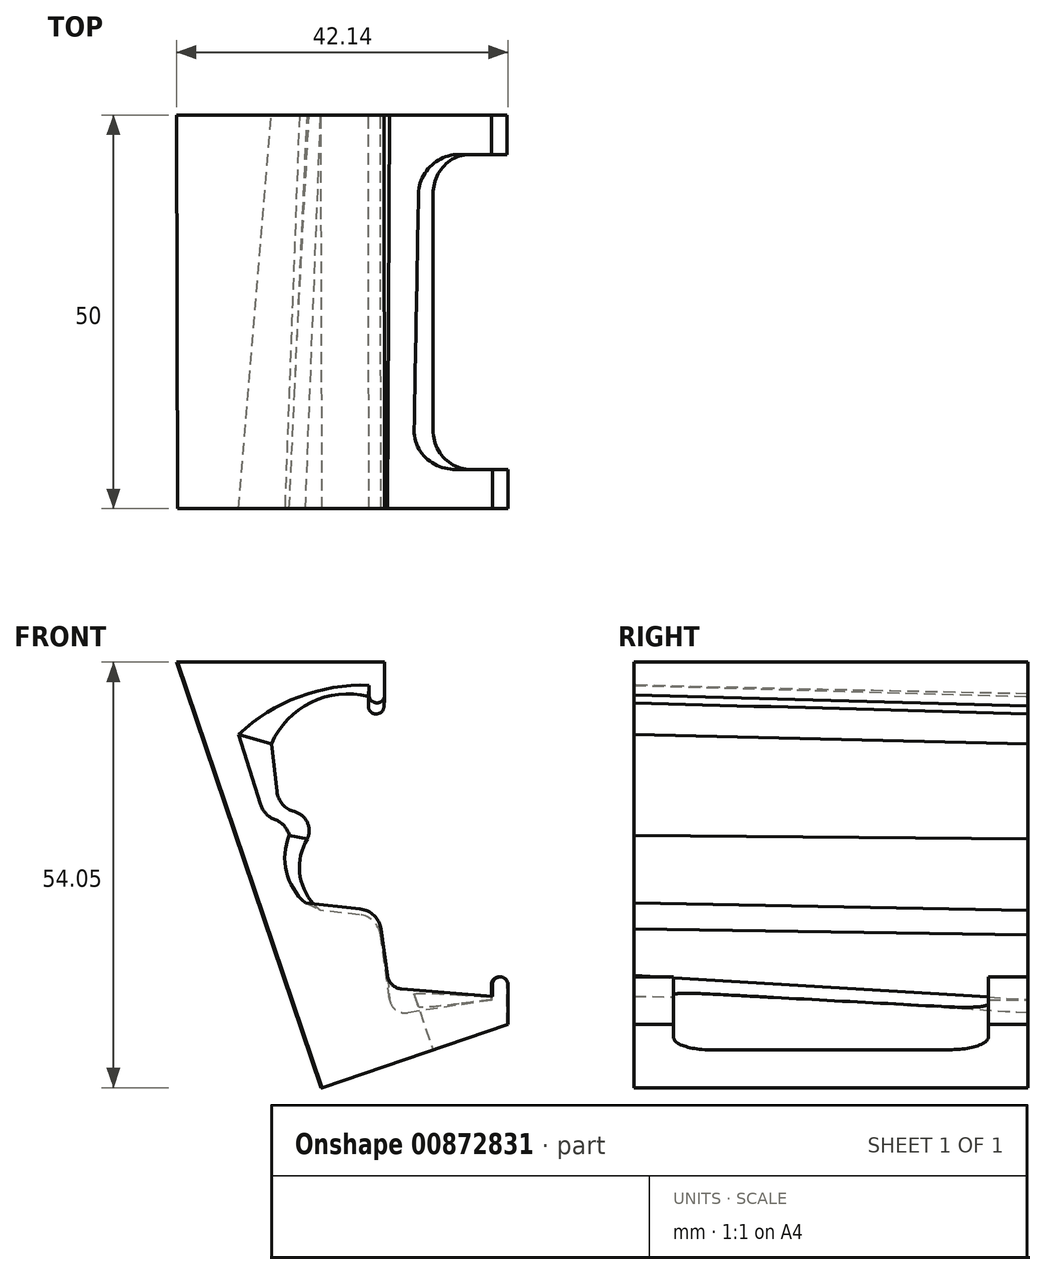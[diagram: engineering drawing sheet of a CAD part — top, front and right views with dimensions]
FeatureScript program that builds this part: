
annotation { "Feature Type Name" : "Feature", "Feature Type Description" : "" }
export const myFeature = defineFeature(function(context is Context, id is Id, definition is map)
    precondition{}
    {
        {
            var Q0;
            Q0=qCreatedBy(makeId("Front.planeOp"),FACE);
            var sketch = newSketch(context, id + "F0", { "sketchPlane" : qUnion([Q0])});
            skLineSegment(sketch, "E0", {"start": v(26.78, 18.86) * mm, "end": v(26.78, -18.67) * mm, "construction": true});
            skFitSpline(sketch, "E1", {"points": [v(2.02, 19.06) * mm, v(0.43, 19.96) * mm, v(-2.84, 19.7) * mm, v(-7.3, 17.92) * mm, v(-11.02, 14.63) * mm, v(-11.52, 11.68) * mm, v(-11.12, 8.55) * mm, v(-10.27, 5.2) * mm, v(-9.23, 3.76) * mm, v(-8.1, 2.95) * mm, v(-7.5, 1.72) * mm, v(-7.46, -0.5) * mm, v(-7.8, -1.76) * mm, v(-7.9, -3.2) * mm, v(-7.44, -5.3) * mm, v(-5.37, -8.08) * mm, v(-3.03, -8.65) * mm, v(-1.6, -8.65) * mm, v(0, -8.76) * mm, v(1.6, -9.26) * mm, v(2.84, -10.63) * mm, v(3.46, -12.42) * mm, v(3.56, -13.7) * mm, v(3.7, -15.6) * mm, v(4.15, -17.72) * mm, v(4.7, -18.85) * mm, v(8.8, -19.5) * mm, v(14.65, -19.88) * mm], "startDerivative": vector(-47.97, 57.65) * mm, "endDerivative": vector(98.98, -5.54) * mm});
            skSolve(sketch);
        }
        {
            var Q0;
            Q0=qCreatedBy(makeId("Front.planeOp"),FACE);
            var sketch = newSketch(context, id + "F1", { "sketchPlane" : qUnion([Q0])});
            skFitSpline(sketch, "E2.0", {"points": [v(2.02, 19.06) * mm, v(1.5, 19.69) * mm, v(0.48, 20.13) * mm, v(-3.08, 19.87) * mm, v(-7.33, 18.2) * mm, v(-11.52, 14.95) * mm, v(-11.6, 11.64) * mm, v(-11.16, 8.62) * mm, v(-10.48, 5.18) * mm, v(-9.35, 3.7) * mm, v(-7.98, 3.04) * mm, v(-7.37, 1.75) * mm, v(-7.34, -0.53) * mm, v(-7.87, -1.72) * mm, v(-7.95, -3.28) * mm, v(-7.62, -5.37) * mm, v(-5.66, -8.49) * mm, v(-3.04, -8.68) * mm, v(-1.62, -8.63) * mm, v(0.02, -8.7) * mm, v(1.7, -9.1) * mm, v(2.96, -10.55) * mm, v(3.53, -12.41) * mm, v(3.55, -13.71) * mm, v(3.63, -15.62) * mm, v(4.17, -17.68) * mm, v(4.43, -19.3) * mm, v(9.19, -19.5) * mm, v(12.72, -19.77) * mm, v(14.65, -19.88) * mm]});
            skLineSegment(sketch, "E3", {"start": v(2.02, 19.06) * mm, "end": v(2.02, 19.06) * mm});
            skLineSegment(sketch, "E4", {"start": v(3.02, 18.06) * mm, "end": v(3.02, 18.06) * mm});
            skLineSegment(sketch, "E5", {"start": v(4.02, 19.06) * mm, "end": v(4.02, 19.46) * mm});
            skLineSegment(sketch, "E6", {"start": v(1.02, 22.46) * mm, "end": v(-22.37, 22.46) * mm});
            skLineSegment(sketch, "E7", {"start": v(-22.37, 22.46) * mm, "end": v(-4.04, -31.53) * mm});
            skPoint(sketch, "E8.visualSharp", {"position": v(2.02, 18.06) * mm});
            skArc(sketch, "E8.filletArc", {"start": v(2.02, 19.06) * mm, "mid": v(2.31, 18.36) * mm, "end": v(3.02, 18.06) * mm});
            skPoint(sketch, "E9.visualSharp", {"position": v(4.02, 18.06) * mm});
            skArc(sketch, "E9.filletArc", {"start": v(3.02, 18.06) * mm, "mid": v(3.73, 18.36) * mm, "end": v(4.02, 19.06) * mm});
            skPoint(sketch, "E10.visualSharp", {"position": v(4.02, 22.46) * mm});
            skArc(sketch, "E10.filletArc", {"start": v(4.02, 19.46) * mm, "mid": v(3.14, 21.58) * mm, "end": v(1.02, 22.46) * mm});
            skPoint(sketch, "E11.visualSharp", {"position": v(-22.37, 22.46) * mm});
            skLineSegment(sketch, "E12", {"start": v(-11.35, 21.09) * mm, "end": v(-11.35, 13.85) * mm, "construction": true});
            skLineSegment(sketch, "E13", {"start": v(14.65, -19.88) * mm, "end": v(17.63, -20.05) * mm});
            skLineSegment(sketch, "E14", {"start": v(19.63, -18.5) * mm, "end": v(19.63, -23.5) * mm});
            skLineSegment(sketch, "E15", {"start": v(19.63, -23.5) * mm, "end": v(-4.04, -31.53) * mm});
            skLineSegment(sketch, "E16", {"start": v(17.63, -20.05) * mm, "end": v(17.63, -18.5) * mm});
            skArc(sketch, "E17", {"start": v(19.63, -18.5) * mm, "mid": v(18.63, -17.5) * mm, "end": v(17.63, -18.5) * mm});
            skSolve(sketch);
        }
        {
            var Q0;
            Q0=qCreatedBy(makeId("Front.planeOp"),FACE);
            cPlane(context, id + "F2", {"entities" : qUnion([Q0]), "cplaneType" : CPlaneType.OFFSET, "offset" : 50 * mm, "width" : 150 * mm, "height" : 150 * mm});
        }
        {
            var Q0;
            Q0=qCreatedBy(makeId("Front.planeOp"),FACE);
            var sketch = newSketch(context, id + "F3", { "sketchPlane" : qUnion([Q0])});
            skLineSegment(sketch, "E18", {"start": v(17.62, -20.46) * mm, "end": v(7, -22.08) * mm});
            skLineSegment(sketch, "E19", {"start": v(4.71, -20.38) * mm, "end": v(3.56, -12.18) * mm});
            skLineSegment(sketch, "E20", {"start": v(0.92, -9.61) * mm, "end": v(-4.05, -9.06) * mm});
            skPoint(sketch, "E21.visualSharp", {"position": v(5, -22.39) * mm});
            skArc(sketch, "E21.filletArc", {"start": v(4.71, -20.38) * mm, "mid": v(5.5, -21.7) * mm, "end": v(7, -22.08) * mm});
            skPoint(sketch, "E22.visualSharp", {"position": v(3.23, -9.87) * mm});
            skArc(sketch, "E22.filletArc", {"start": v(3.56, -12.18) * mm, "mid": v(2.68, -10.44) * mm, "end": v(0.92, -9.61) * mm});
            skArc(sketch, "E23", {"start": v(-5.75, 0) * mm, "mid": v(-6.64, -4.86) * mm, "end": v(-4.05, -9.06) * mm});
            skLineSegment(sketch, "E24", {"start": v(-9.6, 6.03) * mm, "end": v(-10.31, 12.08) * mm});
            skArc(sketch, "E25", {"start": v(2, 18.13) * mm, "mid": v(-5.27, 17.37) * mm, "end": v(-10.31, 12.08) * mm});
            skArc(sketch, "E26", {"start": v(-5.75, 0) * mm, "mid": v(-5.75, 2.12) * mm, "end": v(-7.38, 3.48) * mm});
            skPoint(sketch, "E27.visualSharp", {"position": v(-9.27, 3.22) * mm});
            skArc(sketch, "E27.filletArc", {"start": v(-9.6, 6.03) * mm, "mid": v(-8.88, 4.42) * mm, "end": v(-7.38, 3.48) * mm});
            skLineSegment(sketch, "E28", {"start": v(17.62, -20.46) * mm, "end": v(17.62, -18.52) * mm});
            skLineSegment(sketch, "E29", {"start": v(19.62, -18.52) * mm, "end": v(19.62, -23.56) * mm});
            skLineSegment(sketch, "E30", {"start": v(19.62, -23.56) * mm, "end": v(-4.01, -31.58) * mm});
            skLineSegment(sketch, "E31", {"start": v(-4.01, -31.58) * mm, "end": v(-22.37, 22.47) * mm});
            skLineSegment(sketch, "E32", {"start": v(-22.37, 22.47) * mm, "end": v(4, 22.47) * mm});
            skArc(sketch, "E33", {"start": v(19.62, -18.52) * mm, "mid": v(18.62, -17.52) * mm, "end": v(17.62, -18.52) * mm});
            skLineSegment(sketch, "E34", {"start": v(4, 22.47) * mm, "end": v(4, 16.9) * mm});
            skLineSegment(sketch, "E35", {"start": v(2, 18.13) * mm, "end": v(2, 16.9) * mm});
            skArc(sketch, "E36", {"start": v(2, 16.9) * mm, "mid": v(3, 15.9) * mm, "end": v(4, 16.9) * mm});
            skSolve(sketch);
        }
        {
            var Q0;
            Q0=qCreatedBy(makeId("Front.planeOp"),FACE);
            cPlane(context, id + "F4", {"entities" : qUnion([Q0]), "cplaneType" : CPlaneType.OFFSET, "offset" : 50 * mm, "width" : 150 * mm, "height" : 150 * mm});
        }
        {
            var Q0;
            Q0=qCreatedBy(id+"F4.planeOp",FACE);
            var sketch = newSketch(context, id + "F5", { "sketchPlane" : qUnion([Q0])});
            skLineSegment(sketch, "E37", {"start": v(17.77, -20) * mm, "end": v(6.25, -19.05) * mm});
            skLineSegment(sketch, "E38", {"start": v(4.43, -17.34) * mm, "end": v(3.6, -11.44) * mm});
            skLineSegment(sketch, "E39", {"start": v(0.96, -8.88) * mm, "end": v(-5.98, -8.11) * mm});
            skPoint(sketch, "E40.visualSharp", {"position": v(4.66, -18.92) * mm});
            skArc(sketch, "E40.filletArc", {"start": v(4.43, -17.34) * mm, "mid": v(5.04, -18.51) * mm, "end": v(6.25, -19.05) * mm});
            skPoint(sketch, "E41.visualSharp", {"position": v(3.28, -9.14) * mm});
            skArc(sketch, "E41.filletArc", {"start": v(3.6, -11.44) * mm, "mid": v(2.72, -9.7) * mm, "end": v(0.96, -8.88) * mm});
            skArc(sketch, "E42", {"start": v(-8.04, 0.48) * mm, "mid": v(-8.4, -4.15) * mm, "end": v(-5.98, -8.11) * mm});
            skLineSegment(sketch, "E43", {"start": v(-11.7, 4.4) * mm, "end": v(-14.46, 13.3) * mm});
            skArc(sketch, "E44", {"start": v(-8.04, 0.48) * mm, "mid": v(-8.72, 1.7) * mm, "end": v(-9.88, 2.49) * mm});
            skPoint(sketch, "E45.visualSharp", {"position": v(-11.16, 2.67) * mm});
            skArc(sketch, "E45.filletArc", {"start": v(-11.7, 4.4) * mm, "mid": v(-11.01, 3.24) * mm, "end": v(-9.88, 2.49) * mm});
            skLineSegment(sketch, "E46", {"start": v(17.77, -20) * mm, "end": v(17.77, -18.52) * mm});
            skLineSegment(sketch, "E47", {"start": v(19.77, -18.52) * mm, "end": v(19.77, -23.56) * mm});
            skLineSegment(sketch, "E48", {"start": v(19.77, -23.56) * mm, "end": v(-3.86, -31.58) * mm});
            skLineSegment(sketch, "E49", {"start": v(-3.86, -31.58) * mm, "end": v(-22.22, 22.47) * mm});
            skLineSegment(sketch, "E50", {"start": v(-22.22, 22.47) * mm, "end": v(4.09, 22.47) * mm});
            skArc(sketch, "E51", {"start": v(19.77, -18.52) * mm, "mid": v(18.77, -17.52) * mm, "end": v(17.77, -18.52) * mm});
            skLineSegment(sketch, "E52", {"start": v(4.09, 22.47) * mm, "end": v(4.09, 18.3) * mm});
            skLineSegment(sketch, "E53", {"start": v(2.09, 19.54) * mm, "end": v(2.09, 18.3) * mm});
            skArc(sketch, "E54", {"start": v(2.09, 18.3) * mm, "mid": v(3.09, 17.3) * mm, "end": v(4.09, 18.3) * mm});
            skArc(sketch, "E55", {"start": v(2.09, 19.54) * mm, "mid": v(-6.8, 18.07) * mm, "end": v(-14.46, 13.3) * mm});
            skSolve(sketch);
        }
        {
            var Q0;
            Q0 = qSketchRegion(id + "F5", true);
            var Q1;
            Q1 = qSketchRegion(id + "F3", true);
            loft(context, id + "F6", {"sheetProfilesArray" : [{ "sheetProfileEntities" : qUnion([Q0]) }, { "sheetProfileEntities" : qUnion([Q1]) }]});
        }
        {
            var Q0;
            Q0=makeQuery(id+"F6.opLoft","SWEPT_FACE",FACE,{"disambiguationData":[OSD([sQuery(id+"F3.wireOp",EDGE,"E29"),sQuery(id+"F3.wireOp",EDGE,"E30"),sQuery(id+"F3.wireOp",EDGE,"E31"),sQuery(id+"F5.wireOp",EDGE,"E47"),sQuery(id+"F5.wireOp",EDGE,"E48"),sQuery(id+"F5.wireOp",EDGE,"E49")])]});
            var sketch = newSketch(context, id + "F7", { "sketchPlane" : qUnion([Q0])});
            skLineSegment(sketch, "E56", {"start": v(11.08, 25.02) * mm, "end": v(16.76, 25) * mm, "construction": true});
            skFitSpline(sketch, "E57.0.2", {"points": [v(10.73, 0.02) * mm, v(10.78, 16.69) * mm, v(10.83, 33.35) * mm, v(10.89, 50.02) * mm]});
            skLineSegment(sketch, "E58", {"start": v(13.08, 45.02) * mm, "end": v(12.96, 5.02) * mm});
            skLineSegment(sketch, "E59", {"start": v(13.08, 45.02) * mm, "end": v(6.1, 45.04) * mm});
            skLineSegment(sketch, "E60", {"start": v(1.08, 40.04) * mm, "end": v(1.08, 10.02) * mm});
            skLineSegment(sketch, "E61", {"start": v(6.08, 5.02) * mm, "end": v(12.96, 5.02) * mm});
            skPoint(sketch, "E62.visualSharp", {"position": v(1.08, 45.06) * mm});
            skArc(sketch, "E62.filletArc", {"start": v(6.1, 45.04) * mm, "mid": v(2.55, 43.58) * mm, "end": v(1.08, 40.04) * mm});
            skPoint(sketch, "E63.visualSharp", {"position": v(1.08, 5.02) * mm});
            skArc(sketch, "E63.filletArc", {"start": v(1.08, 10.02) * mm, "mid": v(2.55, 6.48) * mm, "end": v(6.08, 5.02) * mm});
            skSolve(sketch);
        }
        {
            var Q0;
            Q0 = qSketchRegion(id + "F7", true);
            extrude(context, id + "F8", {"entities" : qUnion([Q0]), "operationType" : NewBodyOperationType.REMOVE, "oppositeDirection" : true, "depth" : 15 * mm, "offsetDistance" : 25 * mm});
        }
    });
